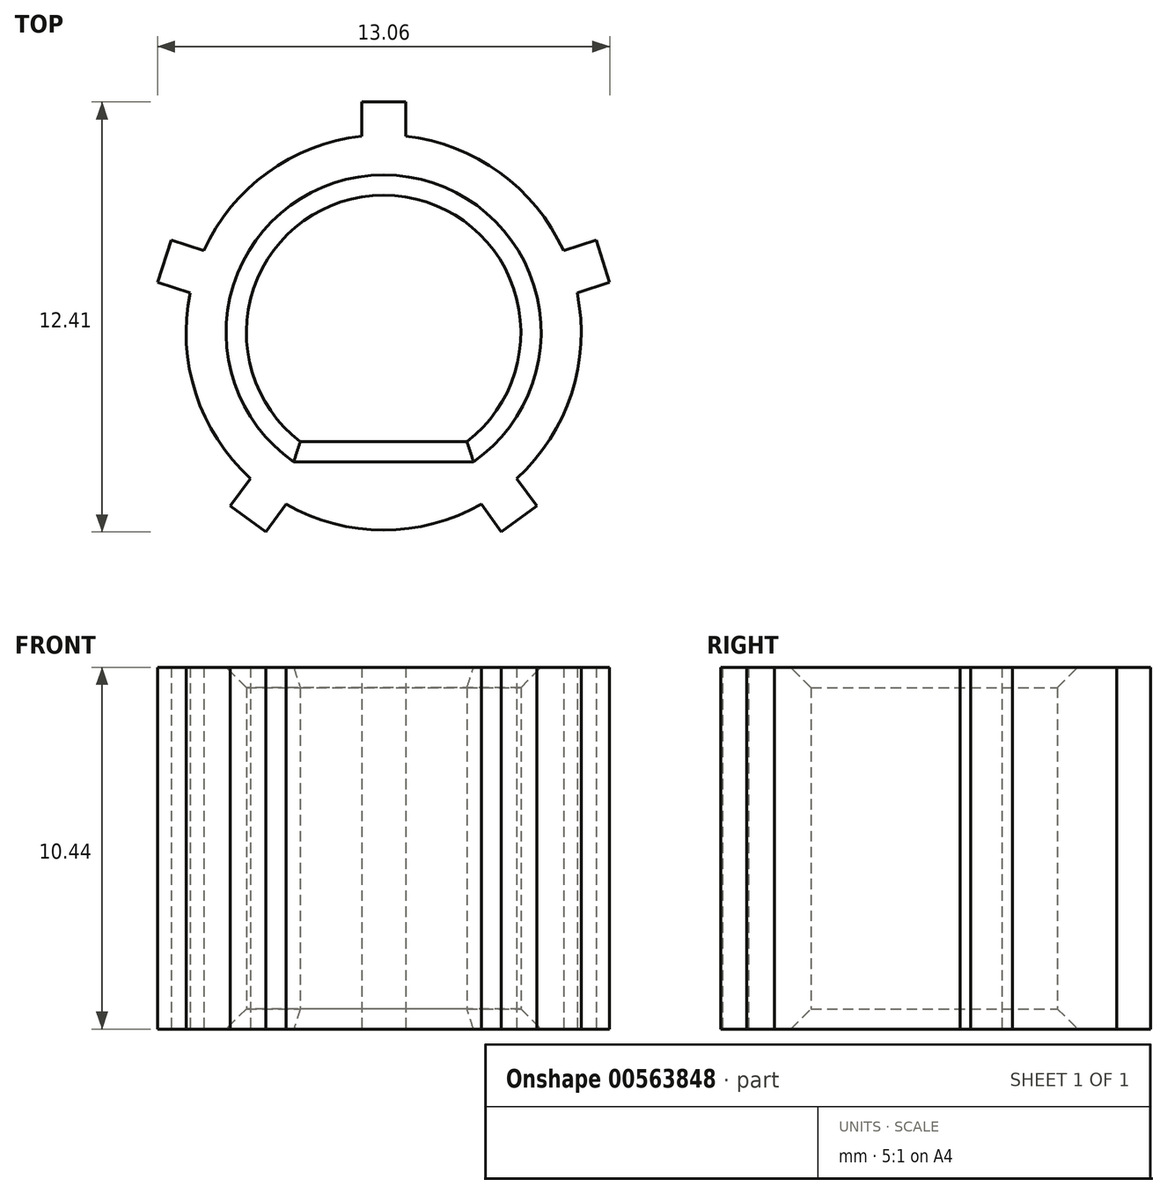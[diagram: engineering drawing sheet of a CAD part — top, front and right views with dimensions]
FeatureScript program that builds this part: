
annotation { "Feature Type Name" : "Feature", "Feature Type Description" : "" }
export const myFeature = defineFeature(function(context is Context, id is Id, definition is map)
    precondition{}
    {
        {
            var Q0;
            Q0=qCreatedBy(makeId("Top.planeOp"),FACE);
            var sketch = newSketch(context, id + "F0", { "sketchPlane" : qUnion([Q0])});
            skArc(sketch, "E0", {"start": v(-5.59, 1.15) * mm, "mid": v(-5.42, -1.76) * mm, "end": v(-3.84, -4.21) * mm});
            skArc(sketch, "E1", {"start": v(2.4, -3.15) * mm, "mid": v(0, 3.96) * mm, "end": v(-2.4, -3.15) * mm});
            skLineSegment(sketch, "E2.trimOffspring", {"start": v(2.4, -3.15) * mm, "end": v(-2.4, -3.15) * mm});
            skLineSegment(sketch, "E3.bottom", {"start": v(0.64, 6.65) * mm, "end": v(-0.64, 6.65) * mm});
            skLineSegment(sketch, "E3.left", {"start": v(0.64, 6.65) * mm, "end": v(0.64, 5.67) * mm});
            skLineSegment(sketch, "E3.right", {"start": v(-0.64, 6.65) * mm, "end": v(-0.64, 5.67) * mm});
            skLineSegment(sketch, "E4.1.0", {"start": v(-6.13, 2.66) * mm, "end": v(-5.2, 2.36) * mm});
            skLineSegment(sketch, "E4.1.1", {"start": v(-6.13, 2.66) * mm, "end": v(-6.53, 1.45) * mm});
            skLineSegment(sketch, "E4.1.2", {"start": v(-6.53, 1.45) * mm, "end": v(-5.59, 1.15) * mm});
            skLineSegment(sketch, "E4.2.0", {"start": v(-4.43, -5.01) * mm, "end": v(-3.84, -4.21) * mm});
            skLineSegment(sketch, "E4.2.1", {"start": v(-4.43, -5.01) * mm, "end": v(-3.4, -5.76) * mm});
            skLineSegment(sketch, "E4.2.2", {"start": v(-3.4, -5.76) * mm, "end": v(-2.82, -4.96) * mm});
            skLineSegment(sketch, "E4.3.0", {"start": v(3.4, -5.76) * mm, "end": v(2.82, -4.96) * mm});
            skLineSegment(sketch, "E4.3.1", {"start": v(3.4, -5.76) * mm, "end": v(4.43, -5.01) * mm});
            skLineSegment(sketch, "E4.3.2", {"start": v(4.43, -5.01) * mm, "end": v(3.84, -4.21) * mm});
            skLineSegment(sketch, "E4.4.0", {"start": v(6.53, 1.45) * mm, "end": v(5.59, 1.15) * mm});
            skLineSegment(sketch, "E4.4.1", {"start": v(6.53, 1.45) * mm, "end": v(6.13, 2.66) * mm});
            skLineSegment(sketch, "E4.4.2", {"start": v(6.13, 2.66) * mm, "end": v(5.2, 2.36) * mm});
            skArc(sketch, "E5.trimOffspring", {"start": v(-0.63, 5.67) * mm, "mid": v(-3.35, 4.61) * mm, "end": v(-5.2, 2.36) * mm});
            skArc(sketch, "E6.trimOffspring", {"start": v(5.2, 2.36) * mm, "mid": v(3.35, 4.61) * mm, "end": v(0.64, 5.67) * mm});
            skArc(sketch, "E7.trimOffspring", {"start": v(3.84, -4.21) * mm, "mid": v(5.42, -1.76) * mm, "end": v(5.59, 1.15) * mm});
            skArc(sketch, "E8.trimOffspring", {"start": v(-2.82, -4.96) * mm, "mid": v(0, -5.7) * mm, "end": v(2.82, -4.96) * mm});
            skSolve(sketch);
        }
        {
            var Q0;
            Q0=makeQuery(id+"F0.imprint","IMPRINT",FACE,{"disambiguationData":[TD([[makeQuery(id+"F0.imprint","IMPRINT",EDGE,{"derivedFrom":sQuery(id+"F0.wireOp",EDGE,"E0")}),1.0]])]});
            extrude(context, id + "F1", {"entities" : qUnion([Q0]), "depth" : 10.44 * mm, "offsetDistance" : 25.4 * mm});
        }
        {
            var Q0;
            Q0=makeQuery(id+"F1.opExtrude","CAP_EDGE",EDGE,{"disambiguationData":[OSD([sQuery(id+"F0.wireOp",EDGE,"E1")])],"isStart":false});
            var Q1;
            Q1=makeQuery(id+"F1.opExtrude","CAP_EDGE",EDGE,{"disambiguationData":[OSD([sQuery(id+"F0.wireOp",EDGE,"E2.trimOffspring")])],"isStart":false});
            var Q2;
            Q2=makeQuery(id+"F1.opExtrude","CAP_EDGE",EDGE,{"disambiguationData":[OSD([sQuery(id+"F0.wireOp",EDGE,"E2.trimOffspring")])],"isStart":true});
            var Q3;
            Q3=makeQuery(id+"F1.opExtrude","CAP_EDGE",EDGE,{"disambiguationData":[OSD([sQuery(id+"F0.wireOp",EDGE,"E1")])],"isStart":true});
            chamfer(context, id + "F2", {"entities" : qUnion([Q0, Q1, Q2, Q3]), "width" : 0.58 * mm, "tangentPropagation" : true});
        }
    });
